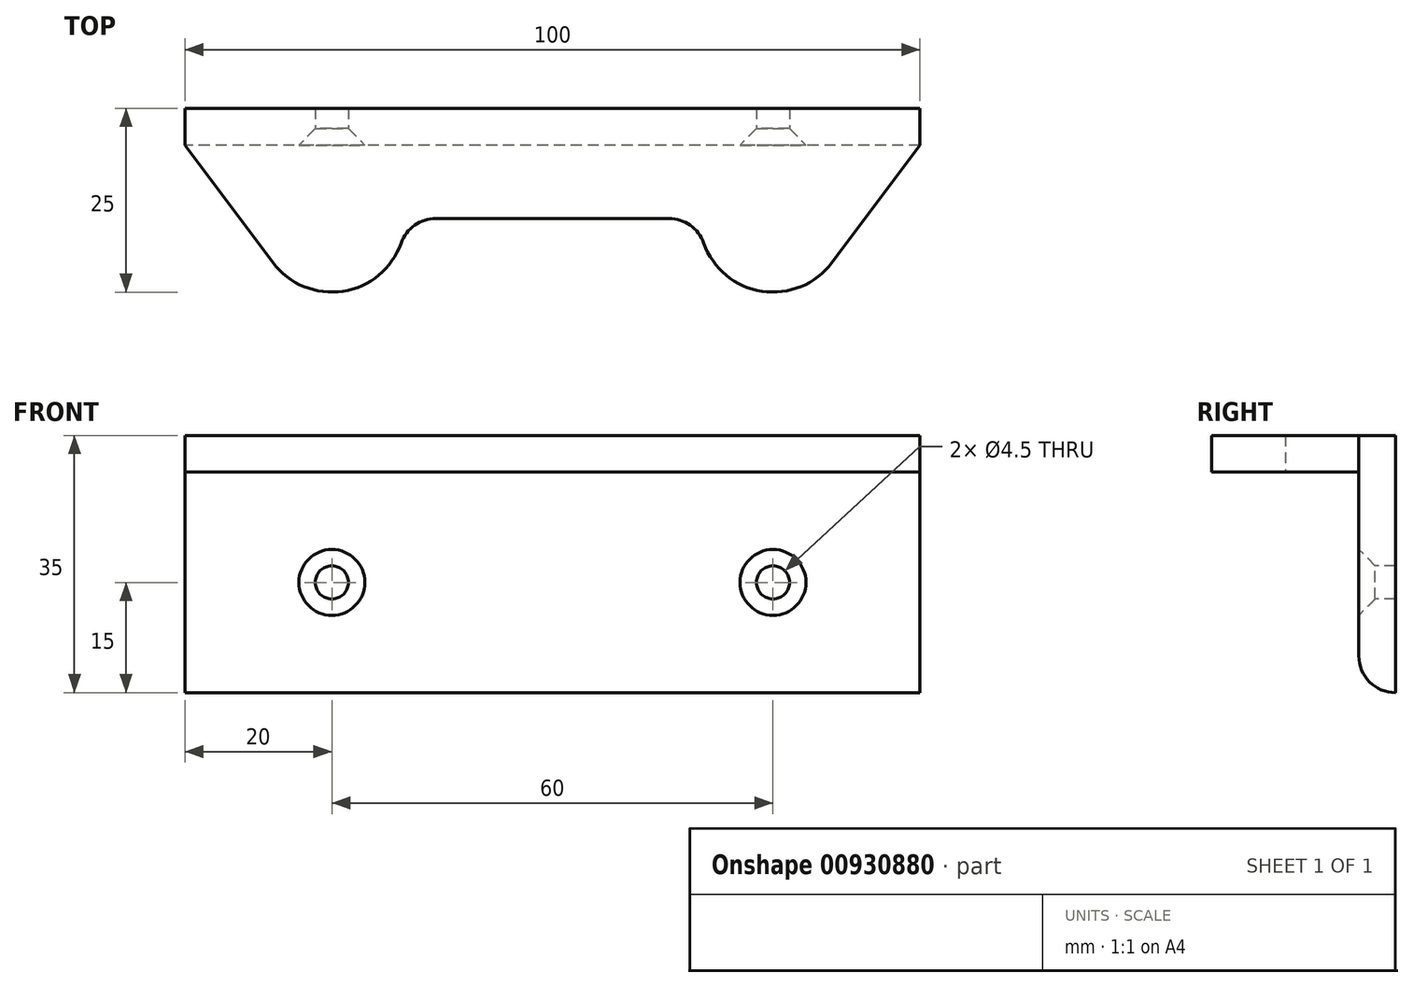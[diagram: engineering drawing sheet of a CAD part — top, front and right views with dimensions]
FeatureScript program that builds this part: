
annotation { "Feature Type Name" : "Feature", "Feature Type Description" : "" }
export const myFeature = defineFeature(function(context is Context, id is Id, definition is map)
    precondition{}
    {
        {
            var Q0;
            Q0=qCreatedBy(makeId("Front.planeOp"),FACE);
            var sketch = newSketch(context, id + "F0", { "sketchPlane" : qUnion([Q0])});
            skLineSegment(sketch, "E0", {"start": v(-50, 25) * mm, "end": v(50, 25) * mm});
            skLineSegment(sketch, "E1", {"start": v(50, 25) * mm, "end": v(50, -10) * mm});
            skLineSegment(sketch, "E2", {"start": v(50, -10) * mm, "end": v(-50, -10) * mm});
            skLineSegment(sketch, "E3", {"start": v(-50, 25) * mm, "end": v(-50, -10) * mm});
            skPoint(sketch, "E4", {"position": v(-30, 5) * mm});
            skPoint(sketch, "E5", {"position": v(30, 5) * mm});
            skSolve(sketch);
        }
        {
            var Q0;
            Q0 = qSketchRegion(id + "F0", true);
            extrude(context, id + "F1", {"entities" : qUnion([Q0]), "depth" : 5 * mm, "offsetDistance" : 25 * mm});
        }
        {
            var Q0;
            Q0=makeQuery(id+"F1.opExtrude","SWEPT_FACE",FACE,{"disambiguationData":[OSD([sQuery(id+"F0.wireOp",EDGE,"E0")])]});
            var sketch = newSketch(context, id + "F2", { "sketchPlane" : qUnion([Q0])});
            skLineSegment(sketch, "E6", {"start": v(-69.8, -15) * mm, "end": v(65.13, -15) * mm, "construction": true});
            skLineSegment(sketch, "E7", {"start": v(-30, 10.57) * mm, "end": v(-30, -28.9) * mm, "construction": true});
            skLineSegment(sketch, "E8", {"start": v(30, 11.64) * mm, "end": v(30, -28.9) * mm, "construction": true});
            skArc(sketch, "E9", {"start": v(-38, -21) * mm, "mid": v(-26.84, -24.49) * mm, "end": v(-20, -15) * mm});
            skArc(sketch, "E10", {"start": v(20, -15) * mm, "mid": v(30, -25) * mm, "end": v(40, -15) * mm});
            skLineSegment(sketch, "E11", {"start": v(-20, -15) * mm, "end": v(20, -15) * mm});
            skLineSegment(sketch, "E12", {"start": v(-50, -5) * mm, "end": v(-38, -21) * mm});
            skLineSegment(sketch, "E13", {"start": v(50, -5) * mm, "end": v(38, -21) * mm});
            skSolve(sketch);
        }
        {
            var Q0;
            Q0=makeQuery(id+"F2.imprint","IMPRINT",FACE,{"disambiguationData":[TD([[makeQuery(id+"F2.imprint","IMPRINT",EDGE,{"derivedFrom":sQuery(id+"F2.wireOp",EDGE,"E9")}),1.0]])]});
            extrude(context, id + "F3", {"entities" : qUnion([Q0]), "operationType" : NewBodyOperationType.ADD, "oppositeDirection" : true, "depth" : 5 * mm, "offsetDistance" : 25 * mm});
        }
        {
            var Q0;
            Q0=makeQuery(id+"F3.opExtrude","SWEPT_EDGE",EDGE,{"disambiguationData":[OSD([sQuery(id+"F2.wireOp",EDGE,"E9"),sQuery(id+"F2.wireOp",EDGE,"E11")])]});
            var Q1;
            Q1=makeQuery(id+"F3.opExtrude","CAP_EDGE",EDGE,{"disambiguationData":[OSD([sQuery(id+"F0.wireOp",EDGE,"E0")])],"isStart":false});
            var Q2;
            Q2=makeQuery(id+"F3.opExtrude","SWEPT_EDGE",EDGE,{"disambiguationData":[OSD([sQuery(id+"F2.wireOp",EDGE,"E10"),sQuery(id+"F2.wireOp",EDGE,"E11")])]});
            fillet(context, id + "F4", {"entities" : qUnion([Q0, Q1, Q2]), "radius" : 5 * mm, "tangentPropagation" : true, "allowEdgeOverflow" : false});
        }
        {
            var Q0;
            Q0=makeQuery(id+"F1.opExtrude","CAP_EDGE",EDGE,{"disambiguationData":[OSD([sQuery(id+"F0.wireOp",EDGE,"E2")])],"isStart":false});
            fillet(context, id + "F5", {"entities" : qUnion([Q0]), "radius" : 5 * mm, "tangentPropagation" : true, "allowEdgeOverflow" : false});
        }
        {
            var Q0;
            Q0=makeQuery(id+"F1.opExtrude","CAP_FACE",FACE,{"disambiguationData":[OSD([sQuery(id+"F0.wireOp",EDGE,"E0"),sQuery(id+"F0.wireOp",EDGE,"E1"),sQuery(id+"F0.wireOp",EDGE,"E2"),sQuery(id+"F0.wireOp",EDGE,"E3")])],"isStart":false});
            var sketch = newSketch(context, id + "F6", { "sketchPlane" : qUnion([Q0])});
            skLineSegment(sketch, "E14", {"start": v(-30, 32.8) * mm, "end": v(-30, -22.22) * mm, "construction": true});
            skLineSegment(sketch, "E15", {"start": v(30, 34.3) * mm, "end": v(30, -22.22) * mm, "construction": true});
            skLineSegment(sketch, "E16", {"start": v(-57.15, 5) * mm, "end": v(60.36, 5) * mm, "construction": true});
            skPoint(sketch, "E17", {"position": v(-30, 5) * mm});
            skPoint(sketch, "E18", {"position": v(30, 5) * mm});
            skSolve(sketch);
        }
        {
            var Q0;
            Q0=sQuery(id+"F6.wireOp",VERTEX,"E17");
            var Q1;
            Q1=sQuery(id+"F6.wireOp",VERTEX,"E18");
            var Q2;
            Q2=makeQuery(id+"F1.opExtrude","SWEPT_BODY",BODY,{"disambiguationData":[OSD([sQuery(id+"F0.wireOp",EDGE,"E0"),sQuery(id+"F0.wireOp",EDGE,"E1"),sQuery(id+"F0.wireOp",EDGE,"E2"),sQuery(id+"F0.wireOp",EDGE,"E3")])]});
            hole(context, id + "F7", {"style" : HoleStyle.C_SINK, "endStyle" : HoleEndStyle.THROUGH, "standardTappedOrClearance" : lookupTablePath({ "fit" : "Normal", "standard" : "ISO", "size" : "M4", "type" : "Clearance" }), "standardBlindInLast" : lookupTablePath({ "fit" : "Normal", "standard" : "ISO", "engagement" : "75%", "pitch" : "0.7 mm", "size" : "M4", "type" : "Clearance & tapped" }), "holeDiameter" : 4.5 * mm, "cSinkDiameter" : 8.96 * mm, "cSinkAngle" : 90 * degree, "majorDiameter" : 5 * mm, "isTappedThrough" : true, "tappedDepth" : 12 * mm, "tapClearance" : 3, "startFromSketch" : true, "locations" : qUnion([Q0, Q1]), "scope" : qUnion([Q2])});
        }
    });
